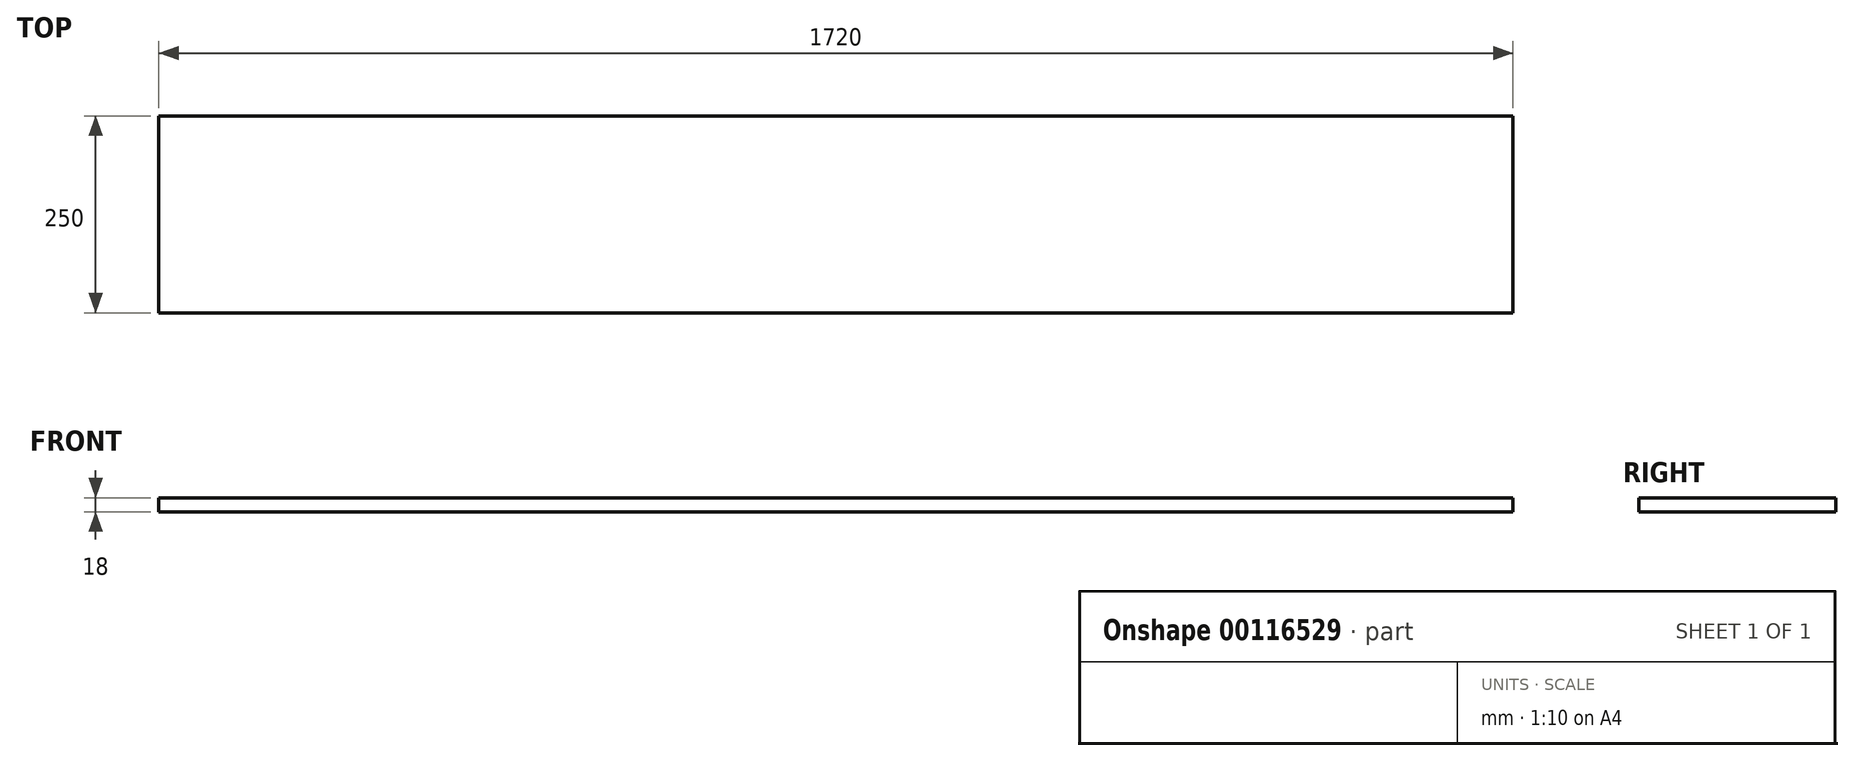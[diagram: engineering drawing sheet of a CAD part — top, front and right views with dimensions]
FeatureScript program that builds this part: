
annotation { "Feature Type Name" : "Feature", "Feature Type Description" : "" }
export const myFeature = defineFeature(function(context is Context, id is Id, definition is map)
    precondition{}
    {
        {
            var Q0;
            Q0=qCreatedBy(makeId("Top.planeOp"),FACE);
            var sketch = newSketch(context, id + "F0", { "sketchPlane" : qUnion([Q0])});
            skLineSegment(sketch, "E0.bottom", {"start": v(-57.48, 285.12) * mm, "end": v(1662.52, 285.12) * mm});
            skLineSegment(sketch, "E0.top", {"start": v(-57.48, 35.12) * mm, "end": v(1662.52, 35.12) * mm});
            skLineSegment(sketch, "E0.left", {"start": v(-57.48, 285.12) * mm, "end": v(-57.48, 35.12) * mm});
            skLineSegment(sketch, "E0.right", {"start": v(1662.52, 285.12) * mm, "end": v(1662.52, 35.12) * mm});
            skLineSegment(sketch, "E1", {"start": v(-57.48, 285.12) * mm, "end": v(192.52, 35.12) * mm});
            skSolve(sketch);
        }
        {
            var Q0;
            Q0=makeQuery(id+"F0.imprint","IMPRINT",FACE,{"disambiguationData":[TD([[makeQuery(id+"F0.imprint","IMPRINT",EDGE,{"derivedFrom":sQuery(id+"F0.wireOp",EDGE,"E0.bottom")}),-1.0]])]});
            var Q1;
            Q1=makeQuery(id+"F0.imprint","IMPRINT",FACE,{"disambiguationData":[TD([[makeQuery(id+"F0.imprint","IMPRINT",EDGE,{"derivedFrom":sQuery(id+"F0.wireOp",EDGE,"E0.bottom")}),-1.0]])]});
            var Q2;
            {var subQ0=sQuery(id+"F0.wireOp",EDGE,"E0.left");Q2=makeQuery(id+"F0.imprint","IMPRINT",FACE,{"disambiguationData":[TD([[makeQuery(id+"F0.imprint","IMPRINT",EDGE,{"derivedFrom":subQ0}),1.0]])]});}
            extrude(context, id + "F1", {"entities" : qUnion([Q0, Q1, Q2]), "depth" : 18 * mm});
        }
    });
